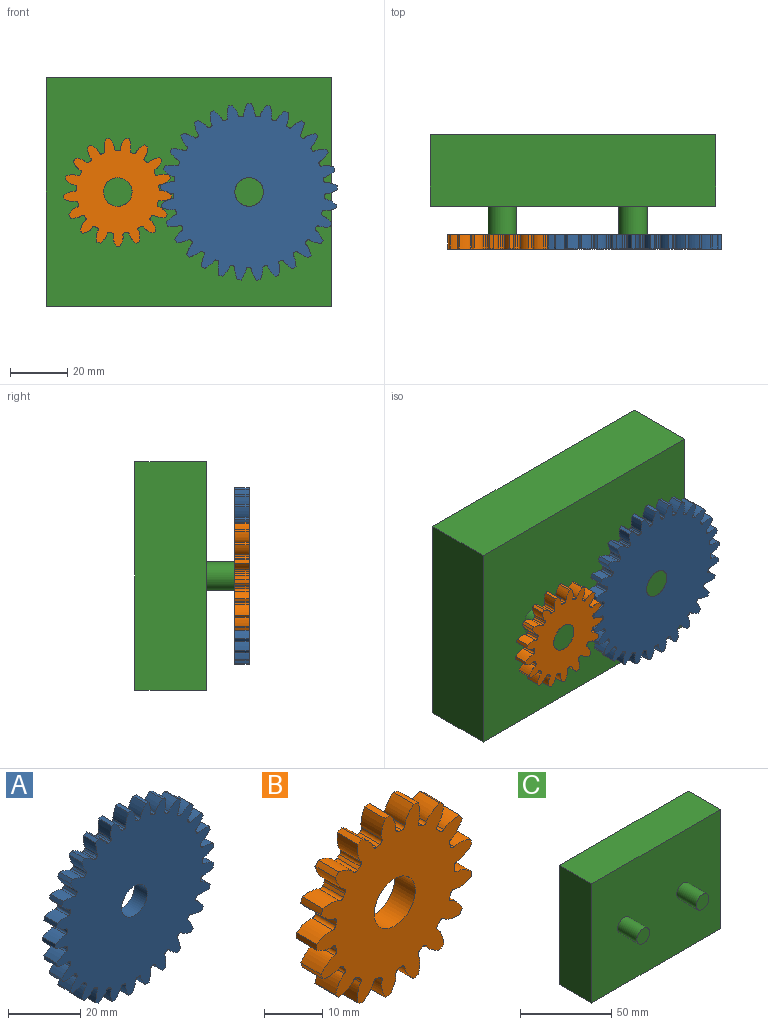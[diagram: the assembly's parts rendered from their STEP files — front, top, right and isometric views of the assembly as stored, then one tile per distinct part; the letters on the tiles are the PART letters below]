
ASSEMBLY  parts=3 mates=2
PART A: 177 faces, bbox 61.9x5x62 mm
  f0: extruded ~5x3.87mm, area 21.4mm2, adj f116,f117,f118,f119
  f1: cylinder r=26.5mm len=5mm, axis (0,1,0), area 3.3mm2, adj f117,f118,f119,f120
  f2: extruded ~5x3.87mm, area 21.4mm2, adj f3,f117,f118,f120
  f3: cylinder r=31mm len=5mm, axis (0,1,0), area 6.6mm2, adj f2,f4,f117,f118
  f4: extruded ~5x4.16mm, area 21.4mm2, adj f3,f117,f118,f121
  f5: cylinder r=26.5mm len=5mm, axis (0,1,0), area 3.3mm2, adj f117,f118,f121,f122
  f6: extruded ~5x3.4mm, area 21.4mm2, adj f7,f117,f118,f122
  f7: cylinder r=31mm len=5mm, axis (0,1,0), area 6.6mm2, adj f6,f8,f117,f118
  f8: extruded ~5x4.25mm, area 21.4mm2, adj f7,f117,f118,f123
  f9: cylinder r=26.5mm len=5mm, axis (0,1,0), area 3.3mm2, adj f117,f118,f123,f124
  f10: extruded ~5x3.23mm, area 21.4mm2, adj f11,f117,f118,f124
  f11: cylinder r=31mm len=5mm, axis (0,1,0), area 6.6mm2, adj f10,f12,f117,f118
  f12: extruded ~5x4.15mm, area 21.4mm2, adj f11,f117,f118,f125
  f13: cylinder r=26.5mm len=5mm, axis (0,1,0), area 3.3mm2, adj f117,f118,f125,f126
  f14: extruded ~5x3.75mm, area 21.4mm2, adj f15,f117,f118,f126
  f15: cylinder r=31mm len=5mm, axis (0,1,0), area 6.6mm2, adj f14,f16,f117,f118
  f16: extruded ~5x3.85mm, area 21.4mm2, adj f15,f117,f118,f127
  f17: cylinder r=26.5mm len=5mm, axis (0,1,0), area 3.3mm2, adj f117,f118,f127,f128
  f18: extruded ~5x4.09mm, area 21.4mm2, adj f19,f117,f118,f128
  f19: cylinder r=31mm len=5mm, axis (0,1,0), area 6.6mm2, adj f18,f20,f117,f118
  f20: extruded ~5x3.37mm, area 21.4mm2, adj f19,f117,f118,f129
  f21: cylinder r=26.5mm len=5mm, axis (0,1,0), area 3.3mm2, adj f117,f118,f129,f130
  f22: extruded ~5x4.25mm, area 21.4mm2, adj f23,f117,f118,f130
  f23: cylinder r=31mm len=5mm, axis (0,1,0), area 6.6mm2, adj f22,f24,f117,f118
  f24: extruded ~5x3.26mm, area 21.4mm2, adj f23,f117,f118,f131
  f25: cylinder r=26.5mm len=5mm, axis (0,1,0), area 3.3mm2, adj f117,f118,f131,f132
  f26: extruded ~5x4.2mm, area 21.4mm2, adj f27,f117,f118,f132
  f27: cylinder r=31mm len=5mm, axis (0,1,0), area 6.6mm2, adj f26,f28,f117,f118
  f28: extruded ~5x3.77mm, area 21.4mm2, adj f27,f117,f118,f133
  f29: cylinder r=26.5mm len=5mm, axis (0,1,0), area 3.3mm2, adj f117,f118,f133,f134
  f30: extruded ~5x3.96mm, area 21.4mm2, adj f31,f117,f118,f134
  f31: cylinder r=31mm len=5mm, axis (0,1,0), area 6.6mm2, adj f30,f32,f117,f118
  f32: extruded ~5x4.1mm, area 21.4mm2, adj f31,f117,f118,f135
  f33: cylinder r=26.5mm len=5mm, axis (0,1,0), area 3.3mm2, adj f117,f118,f135,f136
  f34: extruded ~5x3.53mm, area 21.4mm2, adj f35,f117,f118,f136
  f35: cylinder r=31mm len=5mm, axis (0,1,0), area 6.6mm2, adj f34,f36,f117,f118
  f36: extruded ~5x4.25mm, area 21.4mm2, adj f35,f117,f118,f137
  f37: cylinder r=26.5mm len=5mm, axis (0,1,0), area 3.3mm2, adj f117,f118,f137,f138
  f38: extruded ~5x3.07mm, area 21.4mm2, adj f39,f117,f118,f138
  f39: cylinder r=31mm len=5mm, axis (0,1,0), area 6.6mm2, adj f38,f40,f117,f118
  f40: extruded ~5x4.19mm, area 21.4mm2, adj f39,f117,f118,f139
  f41: cylinder r=26.5mm len=5mm, axis (0,1,0), area 3.3mm2, adj f117,f118,f139,f140
  f42: extruded ~5x3.63mm, area 21.4mm2, adj f43,f117,f118,f140
  f43: cylinder r=31mm len=5mm, axis (0,1,0), area 6.6mm2, adj f42,f44,f117,f118
  f44: extruded ~5x3.94mm, area 21.4mm2, adj f43,f117,f118,f141
  f45: cylinder r=26.5mm len=5mm, axis (0,1,0), area 3.3mm2, adj f117,f118,f141,f142
  f46: extruded ~5x4.02mm, area 21.4mm2, adj f47,f117,f118,f142
  f47: cylinder r=31mm len=5mm, axis (0,1,0), area 6.6mm2, adj f46,f48,f117,f118
  f48: extruded ~5x3.51mm, area 21.4mm2, adj f47,f117,f118,f143
  f49: cylinder r=26.5mm len=5mm, axis (0,1,0), area 3.3mm2, adj f117,f118,f143,f144
  f50: extruded ~5x4.23mm, area 21.4mm2, adj f51,f117,f118,f144
  f51: cylinder r=31mm len=5mm, axis (0,1,0), area 6.6mm2, adj f50,f52,f117,f118
  f52: extruded ~5x3.1mm, area 21.4mm2, adj f51,f117,f118,f145
  f53: cylinder r=26.5mm len=5mm, axis (0,1,0), area 3.3mm2, adj f117,f118,f145,f146
  f54: extruded ~5x4.23mm, area 21.4mm2, adj f55,f117,f118,f146
  f55: cylinder r=31mm len=5mm, axis (0,1,0), area 6.6mm2, adj f54,f56,f117,f118
  f56: extruded ~5x3.66mm, area 21.4mm2, adj f55,f117,f118,f147
  f57: cylinder r=26.5mm len=5mm, axis (0,1,0), area 3.3mm2, adj f117,f118,f147,f148
  f58: extruded ~5x4.04mm, area 21.4mm2, adj f59,f117,f118,f148
  f59: cylinder r=31mm len=5mm, axis (0,1,0), area 6.6mm2, adj f58,f60,f117,f118
  f60: extruded ~5x4.04mm, area 21.4mm2, adj f59,f117,f118,f149
  f61: cylinder r=26.5mm len=5mm, axis (0,1,0), area 3.3mm2, adj f117,f118,f149,f150
  f62: extruded ~5x3.66mm, area 21.4mm2, adj f63,f117,f118,f150
  f63: cylinder r=31mm len=5mm, axis (0,1,0), area 6.6mm2, adj f62,f64,f117,f118
  f64: extruded ~5x4.23mm, area 21.4mm2, adj f63,f117,f118,f151
  f65: cylinder r=26.5mm len=5mm, axis (0,1,0), area 3.3mm2, adj f117,f118,f151,f152
  f66: extruded ~5x3.1mm, area 21.4mm2, adj f67,f117,f118,f152
  f67: cylinder r=31mm len=5mm, axis (0,1,0), area 6.6mm2, adj f66,f68,f117,f118
  f68: extruded ~5x4.23mm, area 21.4mm2, adj f67,f117,f118,f153
  f69: cylinder r=26.5mm len=5mm, axis (0,1,0), area 3.3mm2, adj f117,f118,f153,f154
  f70: extruded ~5x3.51mm, area 21.4mm2, adj f71,f117,f118,f154
  f71: cylinder r=31mm len=5mm, axis (0,1,0), area 6.6mm2, adj f70,f72,f117,f118
  f72: extruded ~5x4.02mm, area 21.4mm2, adj f71,f117,f118,f155
  f73: cylinder r=26.5mm len=5mm, axis (0,1,0), area 3.3mm2, adj f117,f118,f155,f156
  f74: extruded ~5x3.94mm, area 21.4mm2, adj f75,f117,f118,f156
  f75: cylinder r=31mm len=5mm, axis (0,1,0), area 6.6mm2, adj f74,f76,f117,f118
  f76: extruded ~5x3.63mm, area 21.4mm2, adj f75,f117,f118,f157
  f77: cylinder r=26.5mm len=5mm, axis (0,1,0), area 3.3mm2, adj f117,f118,f157,f158
  f78: extruded ~5x4.19mm, area 21.4mm2, adj f79,f117,f118,f158
  f79: cylinder r=31mm len=5mm, axis (0,1,0), area 6.6mm2, adj f78,f80,f117,f118
  f80: extruded ~5x3.07mm, area 21.4mm2, adj f79,f117,f118,f159
  f81: cylinder r=26.5mm len=5mm, axis (0,1,0), area 3.3mm2, adj f117,f118,f159,f160
  f82: extruded ~5x4.25mm, area 21.4mm2, adj f83,f117,f118,f160
  f83: cylinder r=31mm len=5mm, axis (0,1,0), area 6.6mm2, adj f82,f84,f117,f118
  f84: extruded ~5x3.53mm, area 21.4mm2, adj f83,f117,f118,f161
  f85: cylinder r=26.5mm len=5mm, axis (0,1,0), area 3.3mm2, adj f117,f118,f161,f162
  f86: extruded ~5x4.1mm, area 21.4mm2, adj f87,f117,f118,f162
  f87: cylinder r=31mm len=5mm, axis (0,1,0), area 6.6mm2, adj f86,f88,f117,f118
  f88: extruded ~5x3.96mm, area 21.4mm2, adj f87,f117,f118,f163
  f89: cylinder r=26.5mm len=5mm, axis (0,1,0), area 3.3mm2, adj f117,f118,f163,f164
  f90: extruded ~5x3.77mm, area 21.4mm2, adj f91,f117,f118,f164
  f91: cylinder r=31mm len=5mm, axis (0,1,0), area 6.6mm2, adj f90,f92,f117,f118
  f92: extruded ~5x4.2mm, area 21.4mm2, adj f91,f117,f118,f165
  f93: cylinder r=26.5mm len=5mm, axis (0,1,0), area 3.3mm2, adj f117,f118,f165,f166
  f94: extruded ~5x3.26mm, area 21.4mm2, adj f95,f117,f118,f166
  f95: cylinder r=31mm len=5mm, axis (0,1,0), area 6.6mm2, adj f94,f96,f117,f118
  f96: extruded ~5x4.25mm, area 21.4mm2, adj f95,f117,f118,f167
  f97: cylinder r=26.5mm len=5mm, axis (0,1,0), area 3.3mm2, adj f117,f118,f167,f168
  f98: extruded ~5x3.37mm, area 21.4mm2, adj f99,f117,f118,f168
  f99: cylinder r=31mm len=5mm, axis (0,1,0), area 6.6mm2, adj f98,f100,f117,f118
  f100: extruded ~5x4.09mm, area 21.4mm2, adj f99,f117,f118,f169
  f101: cylinder r=26.5mm len=5mm, axis (0,1,0), area 3.3mm2, adj f117,f118,f169,f170
  f102: extruded ~5x3.85mm, area 21.4mm2, adj f103,f117,f118,f170
  f103: cylinder r=31mm len=5mm, axis (0,1,0), area 6.6mm2, adj f102,f104,f117,f118
  f104: extruded ~5x3.75mm, area 21.4mm2, adj f103,f117,f118,f171
  f105: cylinder r=26.5mm len=5mm, axis (0,1,0), area 3.3mm2, adj f117,f118,f171,f172
  f106: extruded ~5x4.15mm, area 21.4mm2, adj f107,f117,f118,f172
  f107: cylinder r=31mm len=5mm, axis (0,1,0), area 6.6mm2, adj f106,f108,f117,f118
  f108: extruded ~5x3.23mm, area 21.4mm2, adj f107,f117,f118,f173
  f109: cylinder r=26.5mm len=5mm, axis (0,1,0), area 3.3mm2, adj f117,f118,f173,f174
  f110: extruded ~5x4.25mm, area 21.4mm2, adj f111,f117,f118,f174
  f111: cylinder r=31mm len=5mm, axis (0,1,0), area 6.6mm2, adj f110,f112,f117,f118
  f112: extruded ~5x3.4mm, area 21.4mm2, adj f111,f117,f118,f175
  f113: cylinder r=26.5mm len=5mm, axis (0,1,0), area 3.3mm2, adj f117,f118,f175,f176
  f114: extruded ~5x4.16mm, area 21.4mm2, adj f116,f117,f118,f176
  f115: cylinder r=5mm len=10mm, axis (0,1,0), area 157.1mm2, adj f117,f118
  f116: cylinder r=31mm len=5mm, axis (0,1,0), area 6.6mm2, adj f0,f114,f117,f118
  f117: plane 61.97x61.88mm, normal (0,-1,0), area 2535.5mm2, adj f0,f1,f2,f3,f4,f5,f6,f7
  f118: plane 61.97x61.88mm, normal (0,1,0), area 2535.5mm2, adj f0,f1,f2,f3,f4,f5,f6,f7
  f119: cylinder r=0.6mm len=5mm, axis (0,1,0), area 4.3mm2, adj f0,f1,f117,f118
  f120: cylinder r=0.6mm len=5mm, axis (0,1,0), area 4.3mm2, adj f1,f2,f117,f118
  f121: cylinder r=0.6mm len=5mm, axis (0,1,0), area 4.3mm2, adj f4,f5,f117,f118
  f122: cylinder r=0.6mm len=5mm, axis (0,1,0), area 4.3mm2, adj f5,f6,f117,f118
  f123: cylinder r=0.6mm len=5mm, axis (0,1,0), area 4.3mm2, adj f8,f9,f117,f118
  f124: cylinder r=0.6mm len=5mm, axis (0,1,0), area 4.3mm2, adj f9,f10,f117,f118
  f125: cylinder r=0.6mm len=5mm, axis (0,1,0), area 4.3mm2, adj f12,f13,f117,f118
  f126: cylinder r=0.6mm len=5mm, axis (0,1,0), area 4.3mm2, adj f13,f14,f117,f118
  f127: cylinder r=0.6mm len=5mm, axis (0,1,0), area 4.3mm2, adj f16,f17,f117,f118
  f128: cylinder r=0.6mm len=5mm, axis (0,1,0), area 4.3mm2, adj f17,f18,f117,f118
  f129: cylinder r=0.6mm len=5mm, axis (0,1,0), area 4.3mm2, adj f20,f21,f117,f118
  f130: cylinder r=0.6mm len=5mm, axis (0,1,0), area 4.3mm2, adj f21,f22,f117,f118
  f131: cylinder r=0.6mm len=5mm, axis (0,1,0), area 4.3mm2, adj f24,f25,f117,f118
  f132: cylinder r=0.6mm len=5mm, axis (0,1,0), area 4.3mm2, adj f25,f26,f117,f118
  f133: cylinder r=0.6mm len=5mm, axis (0,1,0), area 4.3mm2, adj f28,f29,f117,f118
  f134: cylinder r=0.6mm len=5mm, axis (0,1,0), area 4.3mm2, adj f29,f30,f117,f118
  f135: cylinder r=0.6mm len=5mm, axis (0,1,0), area 4.3mm2, adj f32,f33,f117,f118
  f136: cylinder r=0.6mm len=5mm, axis (0,1,0), area 4.3mm2, adj f33,f34,f117,f118
  f137: cylinder r=0.6mm len=5mm, axis (0,1,0), area 4.3mm2, adj f36,f37,f117,f118
  f138: cylinder r=0.6mm len=5mm, axis (0,1,0), area 4.3mm2, adj f37,f38,f117,f118
  f139: cylinder r=0.6mm len=5mm, axis (0,1,0), area 4.3mm2, adj f40,f41,f117,f118
  f140: cylinder r=0.6mm len=5mm, axis (0,1,0), area 4.3mm2, adj f41,f42,f117,f118
  f141: cylinder r=0.6mm len=5mm, axis (0,1,0), area 4.3mm2, adj f44,f45,f117,f118
  f142: cylinder r=0.6mm len=5mm, axis (0,1,0), area 4.3mm2, adj f45,f46,f117,f118
  f143: cylinder r=0.6mm len=5mm, axis (0,1,0), area 4.3mm2, adj f48,f49,f117,f118
  f144: cylinder r=0.6mm len=5mm, axis (0,1,0), area 4.3mm2, adj f49,f50,f117,f118
  f145: cylinder r=0.6mm len=5mm, axis (0,1,0), area 4.3mm2, adj f52,f53,f117,f118
  f146: cylinder r=0.6mm len=5mm, axis (0,1,0), area 4.3mm2, adj f53,f54,f117,f118
  f147: cylinder r=0.6mm len=5mm, axis (0,1,0), area 4.3mm2, adj f56,f57,f117,f118
  f148: cylinder r=0.6mm len=5mm, axis (0,1,0), area 4.3mm2, adj f57,f58,f117,f118
  f149: cylinder r=0.6mm len=5mm, axis (0,1,0), area 4.3mm2, adj f60,f61,f117,f118
  f150: cylinder r=0.6mm len=5mm, axis (0,1,0), area 4.3mm2, adj f61,f62,f117,f118
  f151: cylinder r=0.6mm len=5mm, axis (0,1,0), area 4.3mm2, adj f64,f65,f117,f118
  f152: cylinder r=0.6mm len=5mm, axis (0,1,0), area 4.3mm2, adj f65,f66,f117,f118
  f153: cylinder r=0.6mm len=5mm, axis (0,1,0), area 4.3mm2, adj f68,f69,f117,f118
  f154: cylinder r=0.6mm len=5mm, axis (0,1,0), area 4.3mm2, adj f69,f70,f117,f118
  f155: cylinder r=0.6mm len=5mm, axis (0,1,0), area 4.3mm2, adj f72,f73,f117,f118
  f156: cylinder r=0.6mm len=5mm, axis (0,1,0), area 4.3mm2, adj f73,f74,f117,f118
  f157: cylinder r=0.6mm len=5mm, axis (0,1,0), area 4.3mm2, adj f76,f77,f117,f118
  f158: cylinder r=0.6mm len=5mm, axis (0,1,0), area 4.3mm2, adj f77,f78,f117,f118
  f159: cylinder r=0.6mm len=5mm, axis (0,1,0), area 4.3mm2, adj f80,f81,f117,f118
  f160: cylinder r=0.6mm len=5mm, axis (0,1,0), area 4.3mm2, adj f81,f82,f117,f118
  f161: cylinder r=0.6mm len=5mm, axis (0,1,0), area 4.3mm2, adj f84,f85,f117,f118
  f162: cylinder r=0.6mm len=5mm, axis (0,1,0), area 4.3mm2, adj f85,f86,f117,f118
  f163: cylinder r=0.6mm len=5mm, axis (0,1,0), area 4.3mm2, adj f88,f89,f117,f118
  f164: cylinder r=0.6mm len=5mm, axis (0,1,0), area 4.3mm2, adj f89,f90,f117,f118
  f165: cylinder r=0.6mm len=5mm, axis (0,1,0), area 4.3mm2, adj f92,f93,f117,f118
  f166: cylinder r=0.6mm len=5mm, axis (0,1,0), area 4.3mm2, adj f93,f94,f117,f118
  f167: cylinder r=0.6mm len=5mm, axis (0,1,0), area 4.3mm2, adj f96,f97,f117,f118
  f168: cylinder r=0.6mm len=5mm, axis (0,1,0), area 4.3mm2, adj f97,f98,f117,f118
  f169: cylinder r=0.6mm len=5mm, axis (0,1,0), area 4.3mm2, adj f100,f101,f117,f118
  f170: cylinder r=0.6mm len=5mm, axis (0,1,0), area 4.3mm2, adj f101,f102,f117,f118
  f171: cylinder r=0.6mm len=5mm, axis (0,1,0), area 4.3mm2, adj f104,f105,f117,f118
  f172: cylinder r=0.6mm len=5mm, axis (0,1,0), area 4.3mm2, adj f105,f106,f117,f118
  f173: cylinder r=0.6mm len=5mm, axis (0,1,0), area 4.3mm2, adj f108,f109,f117,f118
  f174: cylinder r=0.6mm len=5mm, axis (0,1,0), area 4.3mm2, adj f109,f110,f117,f118
  f175: cylinder r=0.6mm len=5mm, axis (0,1,0), area 4.3mm2, adj f112,f113,f117,f118
  f176: cylinder r=0.6mm len=5mm, axis (0,1,0), area 4.3mm2, adj f113,f114,f117,f118
PART B: 105 faces, bbox 37.8x5x38 mm
  f0: extruded ~5x3.63mm, area 20.8mm2, adj f68,f69,f70,f71
  f1: cylinder r=14.5mm len=5mm, axis (0,1,0), area 3.8mm2, adj f69,f70,f71,f72
  f2: extruded ~5x3.63mm, area 20.8mm2, adj f3,f69,f70,f72
  f3: cylinder r=19mm len=5mm, axis (0,1,0), area 6mm2, adj f2,f4,f69,f70
  f4: extruded ~5x4.04mm, area 20.8mm2, adj f3,f69,f70,f73
  f5: cylinder r=14.5mm len=5mm, axis (0,1,0), area 3.8mm2, adj f69,f70,f73,f74
  f6: extruded ~5x2.99mm, area 20.8mm2, adj f7,f69,f70,f74
  f7: cylinder r=19mm len=5mm, axis (0,1,0), area 6mm2, adj f6,f8,f69,f70
  f8: extruded ~5x3.9mm, area 20.8mm2, adj f7,f69,f70,f75
  f9: cylinder r=14.5mm len=5mm, axis (0,1,0), area 3.8mm2, adj f69,f70,f75,f76
  f10: extruded ~5x3.78mm, area 20.8mm2, adj f11,f69,f70,f76
  f11: cylinder r=19mm len=5mm, axis (0,1,0), area 6mm2, adj f10,f12,f69,f70
  f12: extruded ~5x3.23mm, area 20.8mm2, adj f11,f69,f70,f77
  f13: cylinder r=14.5mm len=5mm, axis (0,1,0), area 3.8mm2, adj f69,f70,f77,f78
  f14: extruded ~5x4.06mm, area 20.8mm2, adj f15,f69,f70,f78
  f15: cylinder r=19mm len=5mm, axis (0,1,0), area 6mm2, adj f14,f16,f69,f70
  f16: extruded ~5x3.45mm, area 20.8mm2, adj f15,f69,f70,f79
  f17: cylinder r=14.5mm len=5mm, axis (0,1,0), area 3.8mm2, adj f69,f70,f79,f80
  f18: extruded ~5x3.78mm, area 20.8mm2, adj f19,f69,f70,f80
  f19: cylinder r=19mm len=5mm, axis (0,1,0), area 6mm2, adj f18,f20,f69,f70
  f20: extruded ~5x3.99mm, area 20.8mm2, adj f19,f69,f70,f81
  f21: cylinder r=14.5mm len=5mm, axis (0,1,0), area 3.8mm2, adj f69,f70,f81,f82
  f22: extruded ~5x3mm, area 20.8mm2, adj f23,f69,f70,f82
  f23: cylinder r=19mm len=5mm, axis (0,1,0), area 6mm2, adj f22,f24,f69,f70
  f24: extruded ~5x3.99mm, area 20.8mm2, adj f23,f69,f70,f83
  f25: cylinder r=14.5mm len=5mm, axis (0,1,0), area 3.8mm2, adj f69,f70,f83,f84
  f26: extruded ~5x3.63mm, area 20.8mm2, adj f27,f69,f70,f84
  f27: cylinder r=19mm len=5mm, axis (0,1,0), area 6mm2, adj f26,f28,f69,f70
  f28: extruded ~5x3.44mm, area 20.8mm2, adj f27,f69,f70,f85
  f29: cylinder r=14.5mm len=5mm, axis (0,1,0), area 3.8mm2, adj f69,f70,f85,f86
  f30: extruded ~5x4.04mm, area 20.8mm2, adj f31,f69,f70,f86
  f31: cylinder r=19mm len=5mm, axis (0,1,0), area 6mm2, adj f30,f32,f69,f70
  f32: extruded ~5x3.24mm, area 20.8mm2, adj f31,f69,f70,f87
  f33: cylinder r=14.5mm len=5mm, axis (0,1,0), area 3.8mm2, adj f69,f70,f87,f88
  f34: extruded ~5x3.9mm, area 20.8mm2, adj f35,f69,f70,f88
  f35: cylinder r=19mm len=5mm, axis (0,1,0), area 6mm2, adj f34,f36,f69,f70
  f36: extruded ~5x3.9mm, area 20.8mm2, adj f35,f69,f70,f89
  f37: cylinder r=14.5mm len=5mm, axis (0,1,0), area 3.8mm2, adj f69,f70,f89,f90
  f38: extruded ~5x3.24mm, area 20.8mm2, adj f39,f69,f70,f90
  f39: cylinder r=19mm len=5mm, axis (0,1,0), area 6mm2, adj f38,f40,f69,f70
  f40: extruded ~5x4.04mm, area 20.8mm2, adj f39,f69,f70,f91
  f41: cylinder r=14.5mm len=5mm, axis (0,1,0), area 3.8mm2, adj f69,f70,f91,f92
  f42: extruded ~5x3.44mm, area 20.8mm2, adj f43,f69,f70,f92
  f43: cylinder r=19mm len=5mm, axis (0,1,0), area 6mm2, adj f42,f44,f69,f70
  f44: extruded ~5x3.63mm, area 20.8mm2, adj f43,f69,f70,f93
  f45: cylinder r=14.5mm len=5mm, axis (0,1,0), area 3.8mm2, adj f69,f70,f93,f94
  f46: extruded ~5x3.99mm, area 20.8mm2, adj f47,f69,f70,f94
  f47: cylinder r=19mm len=5mm, axis (0,1,0), area 6mm2, adj f46,f48,f69,f70
  f48: extruded ~5x3mm, area 20.8mm2, adj f47,f69,f70,f95
  f49: cylinder r=14.5mm len=5mm, axis (0,1,0), area 3.8mm2, adj f69,f70,f95,f96
  f50: extruded ~5x3.99mm, area 20.8mm2, adj f51,f69,f70,f96
  f51: cylinder r=19mm len=5mm, axis (0,1,0), area 6mm2, adj f50,f52,f69,f70
  f52: extruded ~5x3.78mm, area 20.8mm2, adj f51,f69,f70,f97
  f53: cylinder r=14.5mm len=5mm, axis (0,1,0), area 3.8mm2, adj f69,f70,f97,f98
  f54: extruded ~5x3.45mm, area 20.8mm2, adj f55,f69,f70,f98
  f55: cylinder r=19mm len=5mm, axis (0,1,0), area 6mm2, adj f54,f56,f69,f70
  f56: extruded ~5x4.06mm, area 20.8mm2, adj f55,f69,f70,f99
  f57: cylinder r=14.5mm len=5mm, axis (0,1,0), area 3.8mm2, adj f69,f70,f99,f100
  f58: extruded ~5x3.23mm, area 20.8mm2, adj f59,f69,f70,f100
  f59: cylinder r=19mm len=5mm, axis (0,1,0), area 6mm2, adj f58,f60,f69,f70
  f60: extruded ~5x3.78mm, area 20.8mm2, adj f59,f69,f70,f101
  f61: cylinder r=14.5mm len=5mm, axis (0,1,0), area 3.8mm2, adj f69,f70,f101,f102
  f62: extruded ~5x3.9mm, area 20.8mm2, adj f63,f69,f70,f102
  f63: cylinder r=19mm len=5mm, axis (0,1,0), area 6mm2, adj f62,f64,f69,f70
  f64: extruded ~5x2.99mm, area 20.8mm2, adj f63,f69,f70,f103
  f65: cylinder r=14.5mm len=5mm, axis (0,1,0), area 3.8mm2, adj f69,f70,f103,f104
  f66: extruded ~5x4.04mm, area 20.8mm2, adj f68,f69,f70,f104
  f67: cylinder r=5mm len=10mm, axis (0,1,0), area 157.1mm2, adj f69,f70
  f68: cylinder r=19mm len=5mm, axis (0,1,0), area 6mm2, adj f0,f66,f69,f70
  f69: plane 37.96x37.8mm, normal (0,-1,0), area 807.9mm2, adj f0,f1,f2,f3,f4,f5,f6,f7
  f70: plane 37.96x37.8mm, normal (0,1,0), area 807.9mm2, adj f0,f1,f2,f3,f4,f5,f6,f7
  f71: cylinder r=0.7mm len=5mm, axis (0,1,0), area 5.3mm2, adj f0,f1,f69,f70
  f72: cylinder r=0.7mm len=5mm, axis (0,1,0), area 5.3mm2, adj f1,f2,f69,f70
  f73: cylinder r=0.7mm len=5mm, axis (0,1,0), area 5.3mm2, adj f4,f5,f69,f70
  f74: cylinder r=0.7mm len=5mm, axis (0,1,0), area 5.3mm2, adj f5,f6,f69,f70
  f75: cylinder r=0.7mm len=5mm, axis (0,1,0), area 5.3mm2, adj f8,f9,f69,f70
  f76: cylinder r=0.7mm len=5mm, axis (0,1,0), area 5.3mm2, adj f9,f10,f69,f70
  f77: cylinder r=0.7mm len=5mm, axis (0,1,0), area 5.3mm2, adj f12,f13,f69,f70
  f78: cylinder r=0.7mm len=5mm, axis (0,1,0), area 5.3mm2, adj f13,f14,f69,f70
  f79: cylinder r=0.7mm len=5mm, axis (0,1,0), area 5.3mm2, adj f16,f17,f69,f70
  f80: cylinder r=0.7mm len=5mm, axis (0,1,0), area 5.3mm2, adj f17,f18,f69,f70
  f81: cylinder r=0.7mm len=5mm, axis (0,1,0), area 5.3mm2, adj f20,f21,f69,f70
  f82: cylinder r=0.7mm len=5mm, axis (0,1,0), area 5.3mm2, adj f21,f22,f69,f70
  f83: cylinder r=0.7mm len=5mm, axis (0,1,0), area 5.3mm2, adj f24,f25,f69,f70
  f84: cylinder r=0.7mm len=5mm, axis (0,1,0), area 5.3mm2, adj f25,f26,f69,f70
  f85: cylinder r=0.7mm len=5mm, axis (0,1,0), area 5.3mm2, adj f28,f29,f69,f70
  f86: cylinder r=0.7mm len=5mm, axis (0,1,0), area 5.3mm2, adj f29,f30,f69,f70
  f87: cylinder r=0.7mm len=5mm, axis (0,1,0), area 5.3mm2, adj f32,f33,f69,f70
  f88: cylinder r=0.7mm len=5mm, axis (0,1,0), area 5.3mm2, adj f33,f34,f69,f70
  f89: cylinder r=0.7mm len=5mm, axis (0,1,0), area 5.3mm2, adj f36,f37,f69,f70
  f90: cylinder r=0.7mm len=5mm, axis (0,1,0), area 5.3mm2, adj f37,f38,f69,f70
  f91: cylinder r=0.7mm len=5mm, axis (0,1,0), area 5.3mm2, adj f40,f41,f69,f70
  f92: cylinder r=0.7mm len=5mm, axis (0,1,0), area 5.3mm2, adj f41,f42,f69,f70
  f93: cylinder r=0.7mm len=5mm, axis (0,1,0), area 5.3mm2, adj f44,f45,f69,f70
  f94: cylinder r=0.7mm len=5mm, axis (0,1,0), area 5.3mm2, adj f45,f46,f69,f70
  f95: cylinder r=0.7mm len=5mm, axis (0,1,0), area 5.3mm2, adj f48,f49,f69,f70
  f96: cylinder r=0.7mm len=5mm, axis (0,1,0), area 5.3mm2, adj f49,f50,f69,f70
  f97: cylinder r=0.7mm len=5mm, axis (0,1,0), area 5.3mm2, adj f52,f53,f69,f70
  f98: cylinder r=0.7mm len=5mm, axis (0,1,0), area 5.3mm2, adj f53,f54,f69,f70
  f99: cylinder r=0.7mm len=5mm, axis (0,1,0), area 5.3mm2, adj f56,f57,f69,f70
  f100: cylinder r=0.7mm len=5mm, axis (0,1,0), area 5.3mm2, adj f57,f58,f69,f70
  f101: cylinder r=0.7mm len=5mm, axis (0,1,0), area 5.3mm2, adj f60,f61,f69,f70
  f102: cylinder r=0.7mm len=5mm, axis (0,1,0), area 5.3mm2, adj f61,f62,f69,f70
  f103: cylinder r=0.7mm len=5mm, axis (0,1,0), area 5.3mm2, adj f64,f65,f69,f70
  f104: cylinder r=0.7mm len=5mm, axis (0,1,0), area 5.3mm2, adj f65,f66,f69,f70
PART C: 10 faces, bbox 100x40x80 mm
  f0: plane 80x25mm, normal (-1,0,0), area 2000mm2, adj f1,f3,f4,f5
  f1: plane 100x25mm, normal (0,0,-1), area 2500mm2, adj f0,f2,f4,f5
  f2: plane 80x25mm, normal (1,0,0), area 2000mm2, adj f1,f3,f4,f5
  f3: plane 100x25mm, normal (0,0,1), area 2500mm2, adj f0,f2,f4,f5
  f4: plane 100x80mm, normal (0,-1,0), area 7842.9mm2, adj f0,f1,f2,f3,f6,f8
  f5: plane 100x80mm, normal (0,1,0), area 8000mm2, adj f0,f1,f2,f3
  f6: cylinder r=5mm len=15mm, axis (0,1,0), area 471.2mm2, adj f4,f7
  f7: plane 10x10mm, normal (0,-1,0), area 78.5mm2, adj f6
  f8: cylinder r=5mm len=15mm, axis (0,1,0), area 471.2mm2, adj f4,f9
  f9: plane 10x10mm, normal (0,-1,0), area 78.5mm2, adj f8
PLACE A rot(axis=(0,-1,0),46.3deg) t=(19.6,-17.1,-1.94)mm
PLACE B rot(axis=(0,-1,0),69.2deg) t=(-26.4,-17.1,-1.94)mm
PLACE C t=(-1.4,17.9,-1.94)mm fixed
MATE revolute A.f3 <-> C.f8  axis (0,-1,0) through (19.6,-22.1,-1.94)mm
MATE revolute B.f3 <-> C.f6  axis (0,-1,0) through (-26.4,-22.1,-1.94)mm
